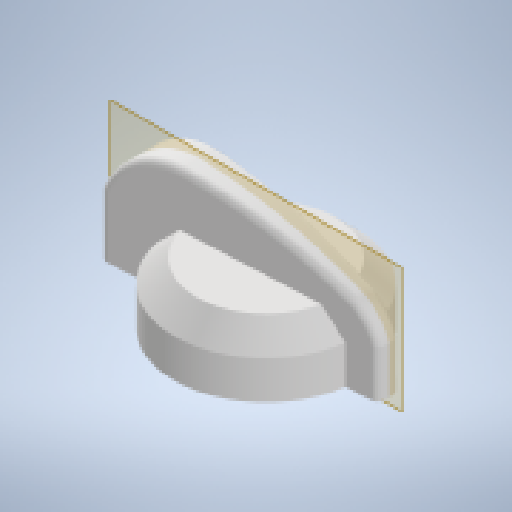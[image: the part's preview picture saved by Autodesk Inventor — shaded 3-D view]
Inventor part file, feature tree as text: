
AUTODESK INVENTOR PART (.ipt)
format: ipt  version: 2023.1 (Build 271208000, 208)  size: 269,312 bytes
history: native  units: in
note: dims shown in document units (in); Inventor stores cm internally (conversion verified against a paired STEP export)
features: extrude x4, sketch x2, chamfer x1, plane x1, fillet x1
ambient origin geometry x8: Origin, YZ Plane, XZ Plane, XY Plane, X Axis, Y Axis, Z Axis, Center Point
bodies: Solid1 (feature_tree)
feature tree (9):
  sketch  "Sketch1"  dims[d0=2.0866in d1=1.5748in]
  extrude  "Extrusion1"  Depth=1.5748in
  extrude  "Extrusion2"  Depth=0.0787in
  chamfer  "Chamfer1"  Distance=0.5709in
  extrude  "Extrusion3"  Depth=0.0787in
  plane  "Work Plane1"
  extrude  "Extrusion4"  Depth=0.0787in TaperAngle=0.0deg
  fillet  "Fillet1"  Radius=0.689in
  sketch  "Sketch2"  dims[d4=0.5315in d5=0.2441in d6=0.5709in d7=0.3425in d8=0.4331in d9=0.0in d10=0.689in d11=0.0in d12=0.2559in d13=0.0787in d14=45.0deg d15=1.2874in d16=0.0in d17=2.6624in d18=0.0in d19=0.0787in d20=0.0344in]
